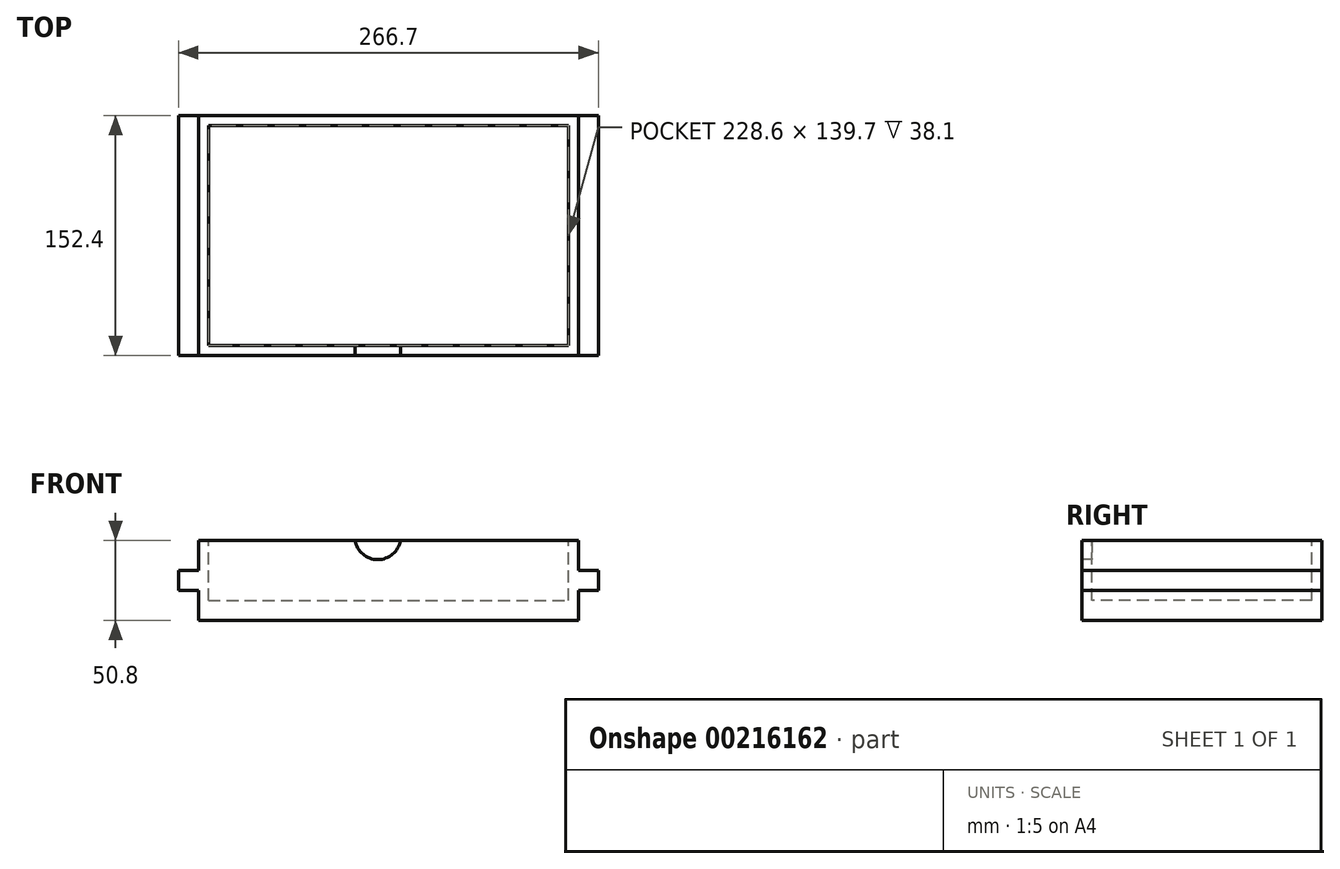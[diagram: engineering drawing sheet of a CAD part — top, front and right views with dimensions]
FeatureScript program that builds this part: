
annotation { "Feature Type Name" : "Feature", "Feature Type Description" : "" }
export const myFeature = defineFeature(function(context is Context, id is Id, definition is map)
    precondition{}
    {
        {
            var Q0;
            Q0=qCreatedBy(makeId("Front.planeOp"),FACE);
            var sketch = newSketch(context, id + "F0", { "sketchPlane" : qUnion([Q0])});
            skLineSegment(sketch, "E0.bottom", {"start": v(-148.32, -18.65) * mm, "end": v(92.98, -18.65) * mm});
            skLineSegment(sketch, "E0.top", {"start": v(-148.32, -69.45) * mm, "end": v(92.98, -69.45) * mm});
            skLineSegment(sketch, "E0.left", {"start": v(-148.32, -18.65) * mm, "end": v(-148.32, -69.45) * mm});
            skLineSegment(sketch, "E0.right", {"start": v(92.98, -18.65) * mm, "end": v(92.98, -69.45) * mm});
            skLineSegment(sketch, "E1.bottom", {"start": v(92.98, -37.7) * mm, "end": v(105.68, -37.7) * mm});
            skLineSegment(sketch, "E1.top", {"start": v(92.98, -50.4) * mm, "end": v(105.68, -50.4) * mm});
            skLineSegment(sketch, "E1.left", {"start": v(92.98, -37.7) * mm, "end": v(92.98, -50.4) * mm});
            skLineSegment(sketch, "E1.right", {"start": v(105.68, -37.7) * mm, "end": v(105.68, -50.4) * mm});
            skLineSegment(sketch, "E2.bottom", {"start": v(-148.32, -37.7) * mm, "end": v(-161.02, -37.7) * mm});
            skLineSegment(sketch, "E2.top", {"start": v(-148.32, -50.4) * mm, "end": v(-161.02, -50.4) * mm});
            skLineSegment(sketch, "E2.left", {"start": v(-148.32, -37.7) * mm, "end": v(-148.32, -50.4) * mm});
            skLineSegment(sketch, "E2.right", {"start": v(-161.02, -37.7) * mm, "end": v(-161.02, -50.4) * mm});
            skSolve(sketch);
        }
        {
            var Q0;
            Q0=makeQuery(id+"F0.imprint","IMPRINT",FACE,{"disambiguationData":[TD([[makeQuery(id+"F0.imprint","IMPRINT",EDGE,{"derivedFrom":sQuery(id+"F0.wireOp",EDGE,"E2.bottom")}),1.0]])]});
            var Q1;
            {var subQ3=sQuery(id+"F0.wireOp",EDGE,"E0.bottom");Q1=makeQuery(id+"F0.imprint","IMPRINT",FACE,{"disambiguationData":[TD([[makeQuery(id+"F0.imprint","IMPRINT",EDGE,{"derivedFrom":subQ3}),-1.0]])]});}
            var Q2;
            Q2=makeQuery(id+"F0.imprint","IMPRINT",FACE,{"disambiguationData":[TD([[makeQuery(id+"F0.imprint","IMPRINT",EDGE,{"derivedFrom":sQuery(id+"F0.wireOp",EDGE,"E1.bottom")}),-1.0]])]});
            extrude(context, id + "F1", {"entities" : qUnion([Q0, Q1, Q2]), "depth" : 152.4 * mm});
        }
        {
            var Q0;
            Q0=makeQuery(id+"F1.opExtrude","SWEPT_FACE",FACE,{"disambiguationData":[OSD([sQuery(id+"F0.wireOp",EDGE,"E0.bottom")])]});
            var sketch = newSketch(context, id + "F2", { "sketchPlane" : qUnion([Q0])});
            skLineSegment(sketch, "E3.bottom", {"start": v(-141.97, -6.35) * mm, "end": v(86.63, -6.35) * mm});
            skLineSegment(sketch, "E3.top", {"start": v(-141.97, -146.05) * mm, "end": v(86.63, -146.05) * mm});
            skLineSegment(sketch, "E3.left", {"start": v(-141.97, -6.35) * mm, "end": v(-141.97, -146.05) * mm});
            skLineSegment(sketch, "E3.right", {"start": v(86.63, -6.35) * mm, "end": v(86.63, -146.05) * mm});
            skSolve(sketch);
        }
        {
            var Q0;
            Q0=makeQuery(id+"F2.imprint","IMPRINT",FACE,{"disambiguationData":[TD([[makeQuery(id+"F2.imprint","IMPRINT",EDGE,{"derivedFrom":sQuery(id+"F2.wireOp",EDGE,"E3.bottom")}),-1.0]])]});
            extrude(context, id + "F3", {"entities" : qUnion([Q0]), "operationType" : NewBodyOperationType.REMOVE, "oppositeDirection" : true, "depth" : 38.1 * mm});
        }
        {
            var Q0;
            Q0=makeQuery(id+"F1.opExtrude","CAP_FACE",FACE,{"disambiguationData":[OSD([sQuery(id+"F0.wireOp",EDGE,"E0.bottom"),sQuery(id+"F0.wireOp",EDGE,"E0.top"),sQuery(id+"F0.wireOp",EDGE,"E0.left"),sQuery(id+"F0.wireOp",EDGE,"E0.right"),sQuery(id+"F0.wireOp",EDGE,"E1.bottom"),sQuery(id+"F0.wireOp",EDGE,"E1.top"),sQuery(id+"F0.wireOp",EDGE,"E1.right"),sQuery(id+"F0.wireOp",EDGE,"E2.bottom"),sQuery(id+"F0.wireOp",EDGE,"E2.top"),sQuery(id+"F0.wireOp",EDGE,"E2.right")])],"isStart":false});
            var sketch = newSketch(context, id + "F4", { "sketchPlane" : qUnion([Q0])});
            skArc(sketch, "E4", {"start": v(-48.87, -18.65) * mm, "mid": v(-34.47, -30.85) * mm, "end": v(-20.08, -18.65) * mm});
            skSolve(sketch);
        }
        {
            var Q0;
            {var subQ0=sQuery(id+"F4.wireOp",EDGE,"E4");Q0=makeQuery(id+"F4.imprint","IMPRINT",FACE,{"disambiguationData":[TD([[makeQuery(id+"F4.imprint","IMPRINT",EDGE,{"derivedFrom":subQ0}),1.0]])]});}
            extrude(context, id + "F5", {"entities" : qUnion([Q0]), "operationType" : NewBodyOperationType.REMOVE, "oppositeDirection" : true, "depth" : 6.35 * mm});
        }
    });
